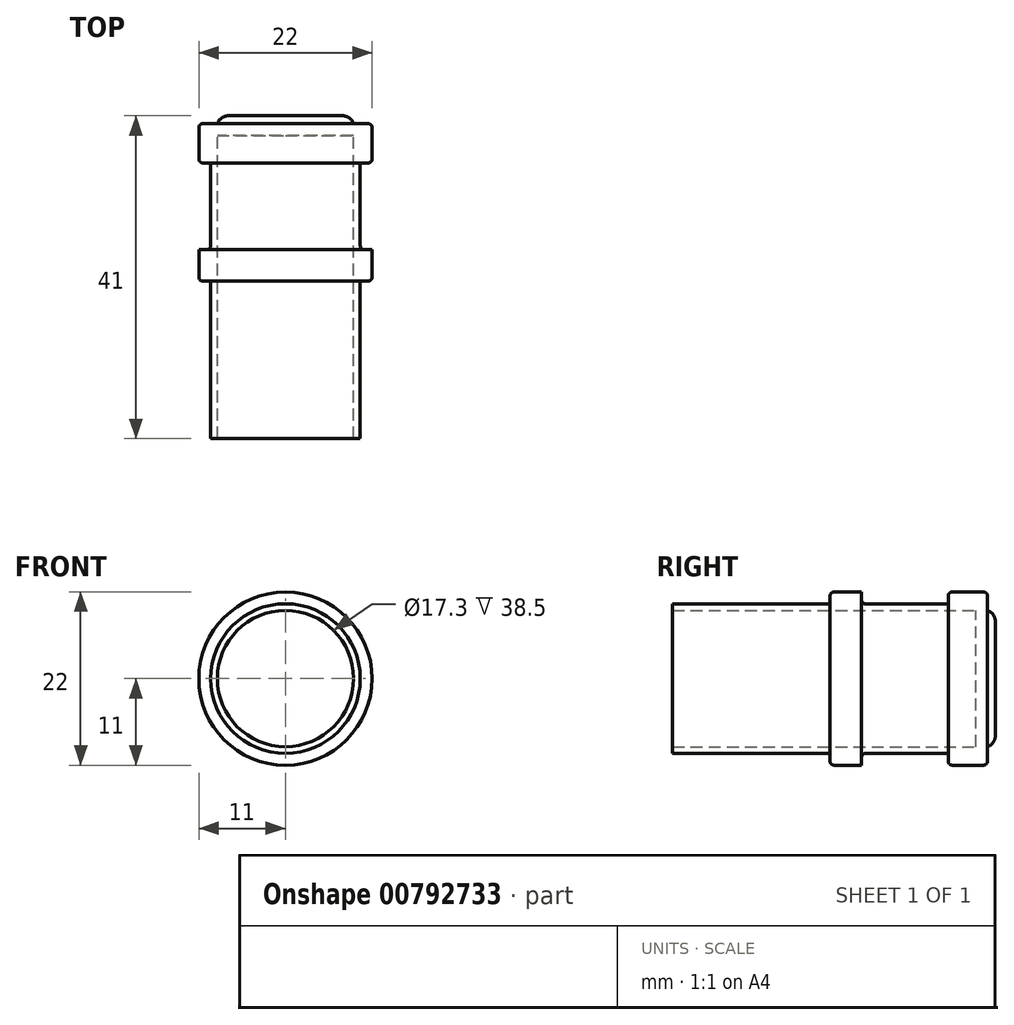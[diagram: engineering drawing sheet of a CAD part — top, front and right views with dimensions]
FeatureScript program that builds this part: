
annotation { "Feature Type Name" : "Feature", "Feature Type Description" : "" }
export const myFeature = defineFeature(function(context is Context, id is Id, definition is map)
    precondition{}
    {
        {
            var Q0;
            Q0=qCreatedBy(makeId("Front.planeOp"),FACE);
            var sketch = newSketch(context, id + "F0", { "sketchPlane" : qUnion([Q0])});
            skCircle(sketch, "E0", {"center": v(0, 0) * mm, "radius": 8.2 * mm});
            skCircle(sketch, "E1", {"center": v(0, 0) * mm, "radius": 8.65 * mm});
            skCircle(sketch, "E2", {"center": v(0, 0) * mm, "radius": 9.5 * mm});
            skCircle(sketch, "E3", {"center": v(0, 0) * mm, "radius": 11 * mm});
            skSolve(sketch);
        }
        {
            var Q0;
            Q0=makeQuery(id+"F0.imprint","IMPRINT",FACE,{"disambiguationData":[TD([[makeQuery(id+"F0.imprint","IMPRINT",EDGE,{"derivedFrom":sQuery(id+"F0.wireOp",EDGE,"E1")}),-1.0]])]});
            extrude(context, id + "F1", {"entities" : qUnion([Q0]), "depth" : 40 * mm, "offsetDistance" : 25 * mm});
        }
        {
            var Q0;
            Q0=makeQuery(id+"F0.imprint","IMPRINT",FACE,{"disambiguationData":[TD([[makeQuery(id+"F0.imprint","IMPRINT",EDGE,{"derivedFrom":sQuery(id+"F0.wireOp",EDGE,"E2")}),-1.0]])]});
            extrude(context, id + "F2", {"entities" : qUnion([Q0]), "operationType" : NewBodyOperationType.ADD, "depth" : 20 * mm, "offsetDistance" : 25 * mm});
        }
        {
            var Q0;
            Q0=makeQuery(id+"F0.imprint","IMPRINT",FACE,{"disambiguationData":[TD([[makeQuery(id+"F0.imprint","IMPRINT",EDGE,{"derivedFrom":sQuery(id+"F0.wireOp",EDGE,"E2")}),-1.0]])]});
            extrude(context, id + "F3", {"entities" : qUnion([Q0]), "operationType" : NewBodyOperationType.REMOVE, "depth" : 16 * mm, "offsetDistance" : 25 * mm});
        }
        {
            var Q0;
            Q0=makeQuery(id+"F0.imprint","IMPRINT",FACE,{"disambiguationData":[TD([[makeQuery(id+"F0.imprint","IMPRINT",EDGE,{"derivedFrom":sQuery(id+"F0.wireOp",EDGE,"E0")}),1.0]])]});
            var sketch = newSketch(context, id + "F4", { "sketchPlane" : qUnion([Q0])});
            skCircle(sketch, "E4", {"center": v(0, 0) * mm, "radius": 11 * mm});
            skCircle(sketch, "E5", {"center": v(0, 0) * mm, "radius": 9.5 * mm});
            skCircle(sketch, "E6", {"center": v(0, 0) * mm, "radius": 8.65 * mm});
            skSolve(sketch);
        }
        {
            var Q0;
            Q0 = qSketchRegion(id + "F4", true);
            extrude(context, id + "F5", {"entities" : qUnion([Q0]), "operationType" : NewBodyOperationType.ADD, "depth" : 5 * mm, "offsetDistance" : 25 * mm});
        }
        {
            var Q0;
            Q0=makeQuery(id+"F5.opExtrude","CAP_EDGE",EDGE,{"disambiguationData":[OSD([sQuery(id+"F4.wireOp",EDGE,"E4")])],"isStart":true});
            var Q1;
            Q1=makeQuery(id+"F5.opExtrude","CAP_EDGE",EDGE,{"disambiguationData":[OSD([sQuery(id+"F4.wireOp",EDGE,"E4")])],"isStart":false});
            var Q2;
            Q2=makeQuery(id+"F3.boolean.opBoolean","COPY",EDGE,{"derivedFrom":makeQuery(id+"F3.opExtrude","CAP_EDGE",EDGE,{"disambiguationData":[OSD([sQuery(id+"F0.wireOp",EDGE,"E3")])],"isStart":false})});
            var Q3;
            Q3=makeQuery(id+"F2.opExtrude","CAP_EDGE",EDGE,{"disambiguationData":[OSD([sQuery(id+"F0.wireOp",EDGE,"E3")])],"isStart":false});
            var Q4;
            Q4=makeQuery(id+"F5.opExtrude","CAP_EDGE",EDGE,{"disambiguationData":[OSD([sQuery(id+"F4.wireOp",EDGE,"E5")])],"isStart":false});
            var Q5;
            Q5=makeQuery(id+"F3.boolean.opBoolean","COPY",EDGE,{"derivedFrom":makeQuery(id+"F3.opExtrude","CAP_EDGE",EDGE,{"disambiguationData":[OSD([sQuery(id+"F0.wireOp",EDGE,"E2")])],"isStart":false})});
            var Q6;
            Q6=makeQuery(id+"F2.opExtrude","CAP_EDGE",EDGE,{"disambiguationData":[OSD([sQuery(id+"F0.wireOp",EDGE,"E2")])],"isStart":false});
            fillet(context, id + "F6", {"entities" : qUnion([Q0, Q1, Q2, Q3, Q4, Q5, Q6]), "radius" : 0.5 * mm, "tangentPropagation" : true, "allowEdgeOverflow" : false});
        }
        {
            var Q0;
            Q0=makeQuery(id+"F4.imprint","IMPRINT",FACE,{"disambiguationData":[TD([[makeQuery(id+"F4.imprint","IMPRINT",EDGE,{"derivedFrom":sQuery(id+"F4.wireOp",EDGE,"E6")}),1.0]])]});
            var Q1;
            Q1=makeQuery(id+"F4.imprint","IMPRINT",FACE,{"disambiguationData":[TD([[makeQuery(id+"F4.imprint","IMPRINT",EDGE,{"derivedFrom":makeQuery(id+"F0.imprint","IMPRINT",EDGE,{"derivedFrom":sQuery(id+"F0.wireOp",EDGE,"E0")})}),1.0]])]});
            extrude(context, id + "F7", {"entities" : qUnion([Q0, Q1]), "operationType" : NewBodyOperationType.ADD, "depth" : 1.5 * mm, "offsetDistance" : 25 * mm});
        }
        {
            var Q0;
            Q0=makeQuery(id+"F4.imprint","IMPRINT",FACE,{"disambiguationData":[TD([[makeQuery(id+"F4.imprint","IMPRINT",EDGE,{"derivedFrom":makeQuery(id+"F0.imprint","IMPRINT",EDGE,{"derivedFrom":sQuery(id+"F0.wireOp",EDGE,"E0")})}),1.0]])]});
            var Q1;
            Q1=makeQuery(id+"F4.imprint","IMPRINT",FACE,{"disambiguationData":[TD([[makeQuery(id+"F4.imprint","IMPRINT",EDGE,{"derivedFrom":sQuery(id+"F4.wireOp",EDGE,"E6")}),1.0]])]});
            extrude(context, id + "F8", {"entities" : qUnion([Q0, Q1]), "operationType" : NewBodyOperationType.ADD, "oppositeDirection" : true, "depth" : 1 * mm, "offsetDistance" : 25 * mm});
        }
        {
            var Q0;
            Q0=makeQuery(id+"F8.opExtrude","CAP_EDGE",EDGE,{"disambiguationData":[OSD([sQuery(id+"F4.wireOp",EDGE,"E6")])],"isStart":false});
            fillet(context, id + "F9", {"entities" : qUnion([Q0]), "radius" : 1.5 * mm, "tangentPropagation" : true, "allowEdgeOverflow" : false});
        }
    });
